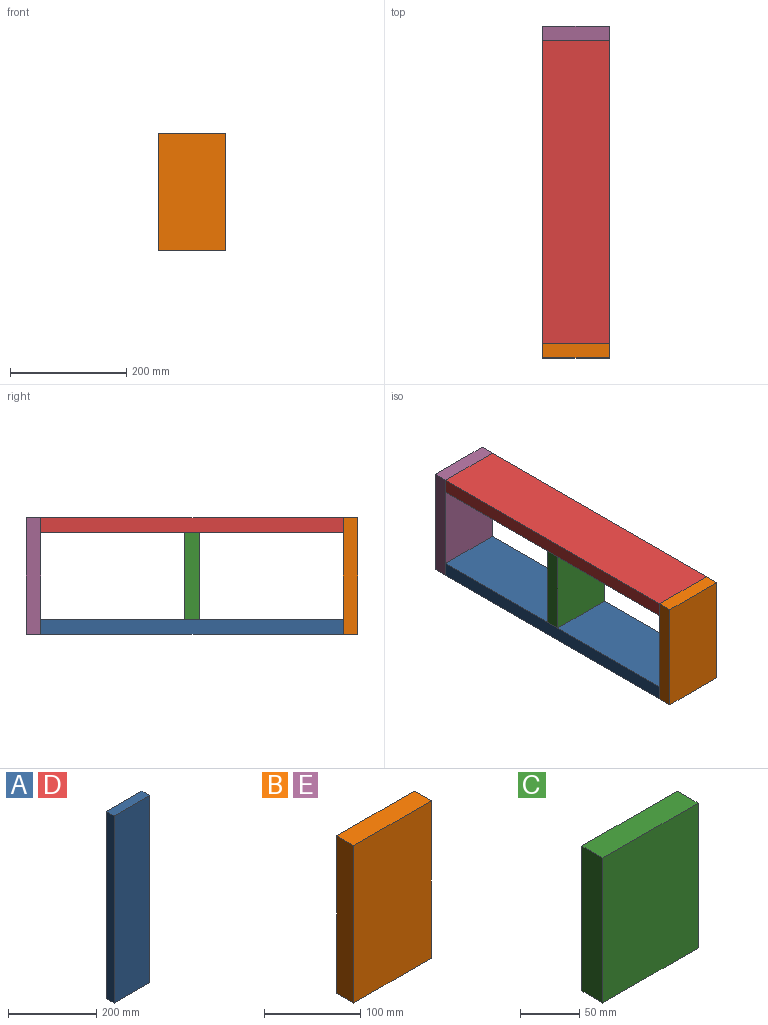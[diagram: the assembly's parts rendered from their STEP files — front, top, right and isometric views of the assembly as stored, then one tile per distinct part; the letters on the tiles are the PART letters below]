
ASSEMBLY  parts=5 mates=4
PART A: 6 faces, bbox 114x25x520 mm
  f0: plane 114x25mm, normal (0,0,1), area 2850mm2, adj f1,f3,f4,f5
  f1: plane 520x25mm, normal (-1,0,0), area 13000mm2, adj f0,f2,f4,f5
  f2: plane 114x25mm, normal (0,0,-1), area 2850mm2, adj f1,f3,f4,f5
  f3: plane 520x25mm, normal (1,0,0), area 13000mm2, adj f0,f2,f4,f5
  f4: plane 520x114mm, normal (0,-1,0), area 59280mm2, adj f0,f1,f2,f3
  f5: plane 520x114mm, normal (0,1,0), area 59280mm2, adj f0,f1,f2,f3
PART B: 6 faces, bbox 114x25x200 mm
  f0: plane 114x25mm, normal (0,0,1), area 2850mm2, adj f1,f3,f4,f5
  f1: plane 200x25mm, normal (-1,0,0), area 5000mm2, adj f0,f2,f4,f5
  f2: plane 114x25mm, normal (0,0,-1), area 2850mm2, adj f1,f3,f4,f5
  f3: plane 200x25mm, normal (1,0,0), area 5000mm2, adj f0,f2,f4,f5
  f4: plane 200x114mm, normal (0,-1,0), area 22800mm2, adj f0,f1,f2,f3
  f5: plane 200x114mm, normal (0,1,0), area 22800mm2, adj f0,f1,f2,f3
PART C: 6 faces, bbox 114x25x150 mm
  f0: plane 114x25mm, normal (0,0,1), area 2850mm2, adj f1,f3,f4,f5
  f1: plane 150x25mm, normal (-1,0,0), area 3750mm2, adj f0,f2,f4,f5
  f2: plane 114x25mm, normal (0,0,-1), area 2850mm2, adj f1,f3,f4,f5
  f3: plane 150x25mm, normal (1,0,0), area 3750mm2, adj f0,f2,f4,f5
  f4: plane 150x114mm, normal (0,-1,0), area 17100mm2, adj f0,f1,f2,f3
  f5: plane 150x114mm, normal (0,1,0), area 17100mm2, adj f0,f1,f2,f3
PART D: same geometry as A
PART E: same geometry as B
PLACE A rot(axis=(1,0,0),90deg) t=(-300.2,14.25,-123.58)mm
PLACE B t=(-1006.98,-402.55,-84.81)mm
PLACE C t=(-1203.08,-130.05,-84.81)mm
PLACE D rot(axis=(1,0,0),90deg) t=(-300.2,14.25,51.42)mm
PLACE E t=(-1006.98,142.45,-84.81)mm
MATE fastened A.f0 <-> B.f5  axis (0,-1,0) through (-526.65,-402.55,-148.58)mm
MATE fastened E.f4 <-> D.f2  axis (0,-1,0) through (-526.65,117.45,51.42)mm
MATE fastened D.f0 <-> B.f5  axis (0,-1,0) through (-526.65,-402.55,51.42)mm
MATE fastened C.f0 <-> D.f4  axis (0,0,1) through (-583.65,-142.55,26.42)mm
